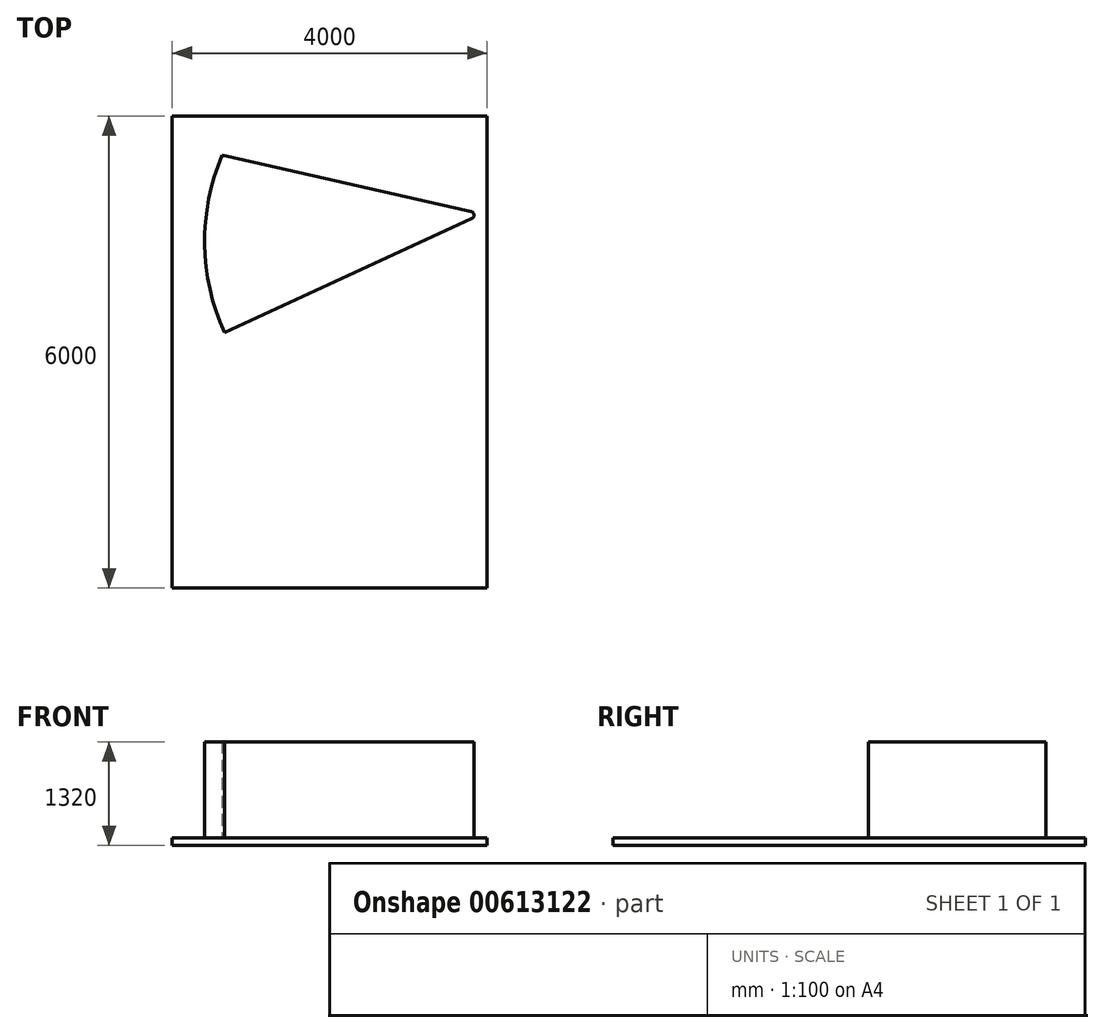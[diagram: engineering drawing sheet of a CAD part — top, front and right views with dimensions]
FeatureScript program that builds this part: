
annotation { "Feature Type Name" : "Feature", "Feature Type Description" : "" }
export const myFeature = defineFeature(function(context is Context, id is Id, definition is map)
    precondition{}
    {
        {
            var Q0;
            Q0=qCreatedBy(makeId("Top.planeOp"),FACE);
            var sketch = newSketch(context, id + "F0", { "sketchPlane" : qUnion([Q0])});
            skLineSegment(sketch, "E0.bottom", {"start": v(-2000, 0) * mm, "end": v(2000, 0) * mm});
            skLineSegment(sketch, "E0.top", {"start": v(-2000, -6000) * mm, "end": v(2000, -6000) * mm});
            skLineSegment(sketch, "E0.left", {"start": v(-2000, 0) * mm, "end": v(-2000, -6000) * mm});
            skLineSegment(sketch, "E0.right", {"start": v(2000, 0) * mm, "end": v(2000, -6000) * mm});
            skSolve(sketch);
        }
        {
            var Q0;
            Q0 = qSketchRegion(id + "F0", true);
            extrude(context, id + "F1", {"entities" : qUnion([Q0]), "oppositeDirection" : true, "depth" : 100 * mm, "offsetDistance" : 25 * mm});
        }
        {
            var Q0;
            Q0=qCreatedBy(makeId("Top.planeOp"),FACE);
            var sketch = newSketch(context, id + "F2", { "sketchPlane" : qUnion([Q0])});
            skLineSegment(sketch, "E1", {"start": v(-1364.93, -499.56) * mm, "end": v(1794.35, -1212.43) * mm});
            skLineSegment(sketch, "E2", {"start": v(1804.28, -1306.61) * mm, "end": v(-1335.28, -2754.13) * mm});
            skArc(sketch, "E3", {"start": v(-1364.93, -499.56) * mm, "mid": v(-1587.52, -1629.97) * mm, "end": v(-1335.28, -2754.13) * mm});
            skPoint(sketch, "E4.visualSharp", {"position": v(1938.17, -1244.88) * mm});
            skArc(sketch, "E4.filletArc", {"start": v(1804.28, -1306.61) * mm, "mid": v(1833.07, -1255.96) * mm, "end": v(1794.35, -1212.43) * mm});
            skSolve(sketch);
        }
        {
            var Q0;
            Q0 = qSketchRegion(id + "F2", true);
            extrude(context, id + "F3", {"entities" : qUnion([Q0]), "depth" : 1220 * mm, "offsetDistance" : 25 * mm});
        }
    });
